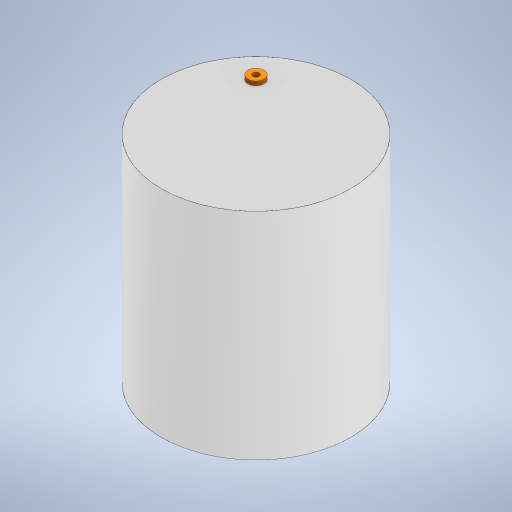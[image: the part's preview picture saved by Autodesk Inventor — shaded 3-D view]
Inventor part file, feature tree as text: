
AUTODESK INVENTOR PART (.ipt)
format: ipt  version: 2024 (Build 280153000, 153)  size: 241,152 bytes
history: native  units: mm
features: extrude x5, sketch x5
ambient origin geometry x8: Origin, YZ Plane, XZ Plane, XY Plane, X Axis, Y Axis, Z Axis, Center Point
bodies: Solid1 (feature_tree)
feature tree (10):
  extrude  "Extrusion1"  Depth=278.0mm
  extrude  "Extrusion2"  Depth=2.0mm TaperAngle=0.0deg
  extrude  "Extrusion3"  Depth=2.0mm
  extrude  "Extrusion9"  Depth=10.0mm
  extrude  "Extrusion10"  Depth=6.0mm TaperAngle=0.0deg
  sketch  "Sketch1"  dims[d0=285.0mm d1=278.0mm]
  sketch  "Sketch2"  dims[d2=320.0mm d3=0.0mm d4=2.0mm d5=0.0mm]
  sketch  "Sketch3"  dims[d6=2.0mm d7=0.0mm d8=14.0mm]
  sketch  "Sketch4"  dims[d23=10.0mm d24=0.0mm d25=9.6mm]
  sketch  "Sketch8"  dims[d26=24.0mm d27=6.0mm d28=0.0mm d11=0.5mm d12=0.872665mm d13=0.5mm d14=0.872665mm]
